# Revit family: LEO_S1_RFA2019
name_source: partatom
category: Mechanical Equipment
units: mm (PartAtom-declared; Revit-internal decimal feet)

## family parameters
Cut with Voids When Loaded = No
Host = Face
Part Type = Normal
Room Calculation Point = No
Round Connector Dimension = Use Diameter
Shared = No

## types (1)
- LEO S1 EPP
    Airflow = 0 m³/h
    Apparent power = 0 VA
    Assembly Code = 51945; LEO S1 EPP 1 řadý výměník (max. 7,8kW; 90/70/15)
    Connection = 1/2"
    Default Elevation = 2500 mm  [stored 8.2021 ft]
    Description = Teplovzdušná jednotka s teplovodním výměníkem
    Fan = axial, single-phase, AC with 3-speed motor
    Heating capacity = 0 kW
    Heating medium flow rate = 0 L/s
    Heating medium pressure drop = 0 kPa
    IP = 54
    Inlet air temperature (Tp1) = 0 °C
    Inlet heating medium temperature (Tw1) = 0 °C
    Load classification = Silnik
    Manufacturer = Hydronic Systems Prague s.r.o.
    Mass of unit = 9.50 kg
    Mass of unit filled with water = 10.20 kg
    Material = EPP-grey
    Max. current consumption = 0 A
    Model = LEO S1
    Outlet air temperature (Tp2) = 0 °C
    Outlet heating medium temperature (Tw2) = 0 °C
    Power factor = 1
    Supply voltage = 230 V
    Type Comments = vnitřní instalace, podstropní/nástěnná; max. teplota okolí +60°C; IP54; twmax=90°C; PN16
    URL = www.hydronic.cz

note: [stored X ft] marks values corroborated as IEEE doubles in the binary element streams (Revit-internal decimal feet)
